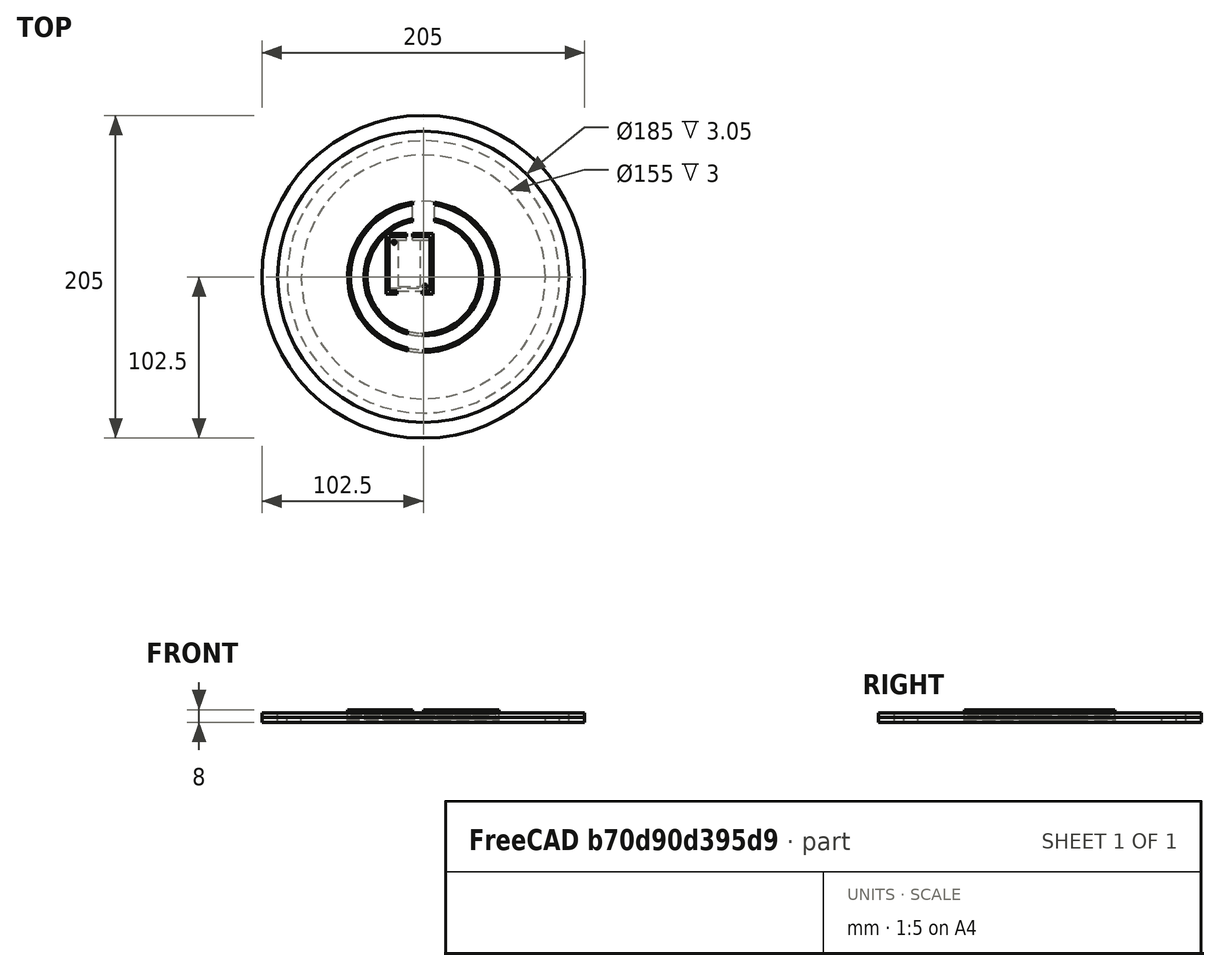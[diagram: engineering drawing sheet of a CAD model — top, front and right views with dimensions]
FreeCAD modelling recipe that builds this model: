
FCSTD DOCUMENT  (FreeCAD 0.19R)
Label: WEMOS-LED-Frame
License: All rights reserved
LicenseURL: http://en.wikipedia.org/wiki/All_rights_reserved
objects: Part::Cylinder×21, Part::Cut×15, Part::Box×13, Part::MultiFuse×2
note: 51 computed .brp shape members not serialized (recipe doc carries the construction recipe); baked Part::Feature solids carry a one-line shape summary decoded from their .brp

FEATURE [Part::Cylinder] Cylinder  label="Astronaut"
  Angle = 360
  AttacherType = Attacher::AttachEngine3D
  Height = 3
  Radius = 92.5
FEATURE [Part::Cylinder] Cylinder001  label="Cylinder"
  Angle = 360
  AttacherType = Attacher::AttachEngine3D
  Height = 3.05
  Radius = 102.5
FEATURE [Part::Cylinder] Cylinder002
  Angle = 360
  AttacherType = Attacher::AttachEngine3D
  Height = 3.05
  Radius = 92.5
FEATURE [Part::Cut] Cut  label="Standoff Base"
  Base = -> Cylinder001
  Placement = pos=(0,0,3.05) rot=(0,0,1;0rad)
  Tool = -> Cylinder002
FEATURE [Part::Cylinder] Cylinder003  label="Backplate Base"
  Angle = 360
  AttacherType = Attacher::AttachEngine3D
  Height = 3.05
  Radius = 102.5
FEATURE [Part::Cylinder] Cylinder004
  Angle = 360
  AttacherType = Attacher::AttachEngine3D
  Height = 3
  Radius = 92.5
FEATURE [Part::Cylinder] Cylinder005
  Angle = 360
  AttacherType = Attacher::AttachEngine3D
  Height = 3
  Placement = pos=(0,0,3) rot=(0,0,1;0rad)
  Radius = 92.5
FEATURE [Part::Cylinder] Cylinder006
  Angle = 360
  AttacherType = Attacher::AttachEngine3D
  Height = 3
  Radius = 77.5
FEATURE [Part::Cylinder] Cylinder007
  Angle = 360
  AttacherType = Attacher::AttachEngine3D
  Height = 3
  Radius = 86.5
FEATURE [Part::Cut] Cut001  label="Large LED Ring"
  Base = -> Cylinder007
  Tool = -> Cylinder006
FEATURE [Part::Cylinder] Cylinder008
  Angle = 360
  AttacherType = Attacher::AttachEngine3D
  Height = 3
  Radius = 46.25
FEATURE [Part::Cylinder] Cylinder009
  Angle = 360
  AttacherType = Attacher::AttachEngine3D
  Height = 3
  Radius = 37.6
FEATURE [Part::Cut] Cut002  label="Small LED Ring"
  Base = -> Cylinder008
  Tool = -> Cylinder009
FEATURE [Part::Cylinder] Cylinder010
  Angle = 360
  AttacherType = Attacher::AttachEngine3D
  Height = 3
  Radius = 48
FEATURE [Part::Cylinder] Cylinder011
  Angle = 360
  AttacherType = Attacher::AttachEngine3D
  Height = 3
  Radius = 35.85
FEATURE [Part::Cut] Cut003
  Base = -> Cylinder010
  Tool = -> Cylinder011
FEATURE [Part::Cut] Cut004
  Base = -> Cut003
  Tool = -> Cut002
FEATURE [Part::Cylinder] Cylinder012
  Angle = 360
  AttacherType = Attacher::AttachEngine3D
  Height = 2
  Placement = pos=(0,0,-2) rot=(0,0,1;0rad)
  Radius = 48
FEATURE [Part::Box] Box  label="Cube"
  AttacherType = Attacher::AttachEngine3D
  Height = 5
  Length = 14
  Placement = pos=(-7,34,-2) rot=(0,0,1;0rad)
  Width = 15
FEATURE [Part::Cut] Cut005
  Base = -> Cut004
  Tool = -> Box
FEATURE [Part::Cylinder] Cylinder013
  Angle = 360
  AttacherType = Attacher::AttachEngine3D
  Height = 2
  Placement = pos=(0,0,-2) rot=(0,0,1;0rad)
  Radius = 35.85
FEATURE [Part::Cut] Cut006
  Base = -> Cylinder012
  Tool = -> Cylinder013
FEATURE [Part::Box] Box001  label="Cube001"
  AttacherType = Attacher::AttachEngine3D
  Height = 5
  Length = 14
  Placement = pos=(-7,34,-2) rot=(0,0,1;0rad)
  Width = 15
FEATURE [Part::Cut] Cut007
  Base = -> Cut006
  Tool = -> Box001
FEATURE [Part::MultiFuse] Fusion  label="Small Ring Track push 1"
  Placement = pos=(0,0,5) rot=(0,0,1;0rad)
  Shapes = -> [Cut007,Cut005]
FEATURE [Part::Box] Box002  label="Cube002"
  AttacherType = Attacher::AttachEngine3D
  Height = 2
  Length = 26
  Width = 34.5
FEATURE [Part::Cylinder] Cylinder014
  Angle = 360
  AttacherType = Attacher::AttachEngine3D
  Height = 3
  Placement = pos=(3.2,31.03,2) rot=(0,0,1;0rad)
  Radius = 1.1
FEATURE [Part::Cylinder] Cylinder015
  Angle = 360
  AttacherType = Attacher::AttachEngine3D
  Height = 3
  Placement = pos=(22.82,2.88,2) rot=(0,0,1;0rad)
  Radius = 1.15
FEATURE [Part::Cylinder] Cylinder016
  Angle = 360
  AttacherType = Attacher::AttachEngine3D
  Height = 2
  Placement = pos=(3.18,31.03,2) rot=(0,0,1;0rad)
  Radius = 1.75
FEATURE [Part::Cylinder] Cylinder017
  Angle = 360
  AttacherType = Attacher::AttachEngine3D
  Height = 2
  Placement = pos=(22.82,2.88,2) rot=(0,0,1;0rad)
  Radius = 1.875
FEATURE [Part::Box] Box003  label="Cube003"
  AttacherType = Attacher::AttachEngine3D
  Height = 2
  Length = 14
  Placement = pos=(6,3,0) rot=(0,0,1;0rad)
  Width = 29.5
FEATURE [Part::Cut] Cut008
  Base = -> Box002
  Tool = -> Box003
FEATURE [Part::Box] Box004  label="Cube004"
  AttacherType = Attacher::AttachEngine3D
  Height = 2
  Length = 26
  Placement = pos=(0,0,2) rot=(0,0,1;0rad)
  Width = 2
FEATURE [Part::Box] Box005  label="Cube005"
  AttacherType = Attacher::AttachEngine3D
  Height = 2
  Length = 26
  Placement = pos=(0,32.5,2) rot=(0,0,1;0rad)
  Width = 2
FEATURE [Part::Box] Box006  label="Cube006"
  AttacherType = Attacher::AttachEngine3D
  Height = 5
  Length = 2
  Placement = pos=(-2,0,0) rot=(0,0,1;0rad)
  Width = 34.5
FEATURE [Part::Box] Box007  label="Cube007"
  AttacherType = Attacher::AttachEngine3D
  Height = 5
  Length = 2
  Placement = pos=(26,0,0) rot=(0,0,1;0rad)
  Width = 34.5
FEATURE [Part::Box] Box008  label="Cube008"
  AttacherType = Attacher::AttachEngine3D
  Height = 5
  Length = 30
  Placement = pos=(-2,34.5,0) rot=(0,0,1;0rad)
  Width = 2
FEATURE [Part::Box] Box009  label="Cube009"
  AttacherType = Attacher::AttachEngine3D
  Height = 5
  Length = 7
  Placement = pos=(-2,-2,0) rot=(0,0,1;0rad)
  Width = 2
FEATURE [Part::Box] Box010  label="Cube010"
  AttacherType = Attacher::AttachEngine3D
  Height = 5
  Length = 7
  Placement = pos=(21,-2,0) rot=(0,0,1;0rad)
  Width = 2
FEATURE [Part::Box] Box011  label="Removal hole"
  AttacherType = Attacher::AttachEngine3D
  Height = 5
  Length = 4
  Placement = pos=(11,32.5,0) rot=(0,0,1;0rad)
  Width = 4
FEATURE [Part::Cut] Cut009
  Base = -> Box005
  Tool = -> Box011
FEATURE [Part::Cut] Cut010
  Base = -> Cut008
  Tool = -> Box011
FEATURE [Part::Cut] Cut011
  Base = -> Box008
  Tool = -> Box011
FEATURE [Part::MultiFuse] Fusion001  label="D1 Stand with Backing"
  Placement = pos=(-21.7,-9,1) rot=(0,0,1;0rad)
  Shapes = -> [Cut011,Cylinder014,Cylinder015,Cylinder016,Cylinder017,Box004,Box006,Box007,Box009,Box010,Cut009,Cut010]
FEATURE [Part::Cylinder] Cylinder018
  Angle = 360
  AttacherType = Attacher::AttachEngine3D
  Height = 2
  Radius = 48
FEATURE [Part::Cylinder] Cylinder019
  Angle = 360
  AttacherType = Attacher::AttachEngine3D
  Height = 1
  Placement = pos=(0,0,2) rot=(0,0,1;0rad)
  Radius = 35.85
FEATURE [Part::Cylinder] Cylinder020
  Angle = 360
  AttacherType = Attacher::AttachEngine3D
  Height = 1
  Placement = pos=(0,0,2) rot=(0,0,1;0rad)
  Radius = 48
FEATURE [Part::Cut] Cut012
  Base = -> Cylinder020
  Tool = -> Cylinder019
FEATURE [Part::Cut] Cut013
  Base = -> Cut012
  Tool = -> Box001
FEATURE [Part::Box] Box012  label="Cube011"
  AttacherType = Attacher::AttachEngine3D
  Height = 3
  Length = 10
  Placement = pos=(-10,-49,5.5) rot=(0,0,1;0rad)
  Width = 16
FEATURE [Part::Cut] Cut014  label="small ring track with USB cut"
  Base = -> Fusion
  Tool = -> Box012
